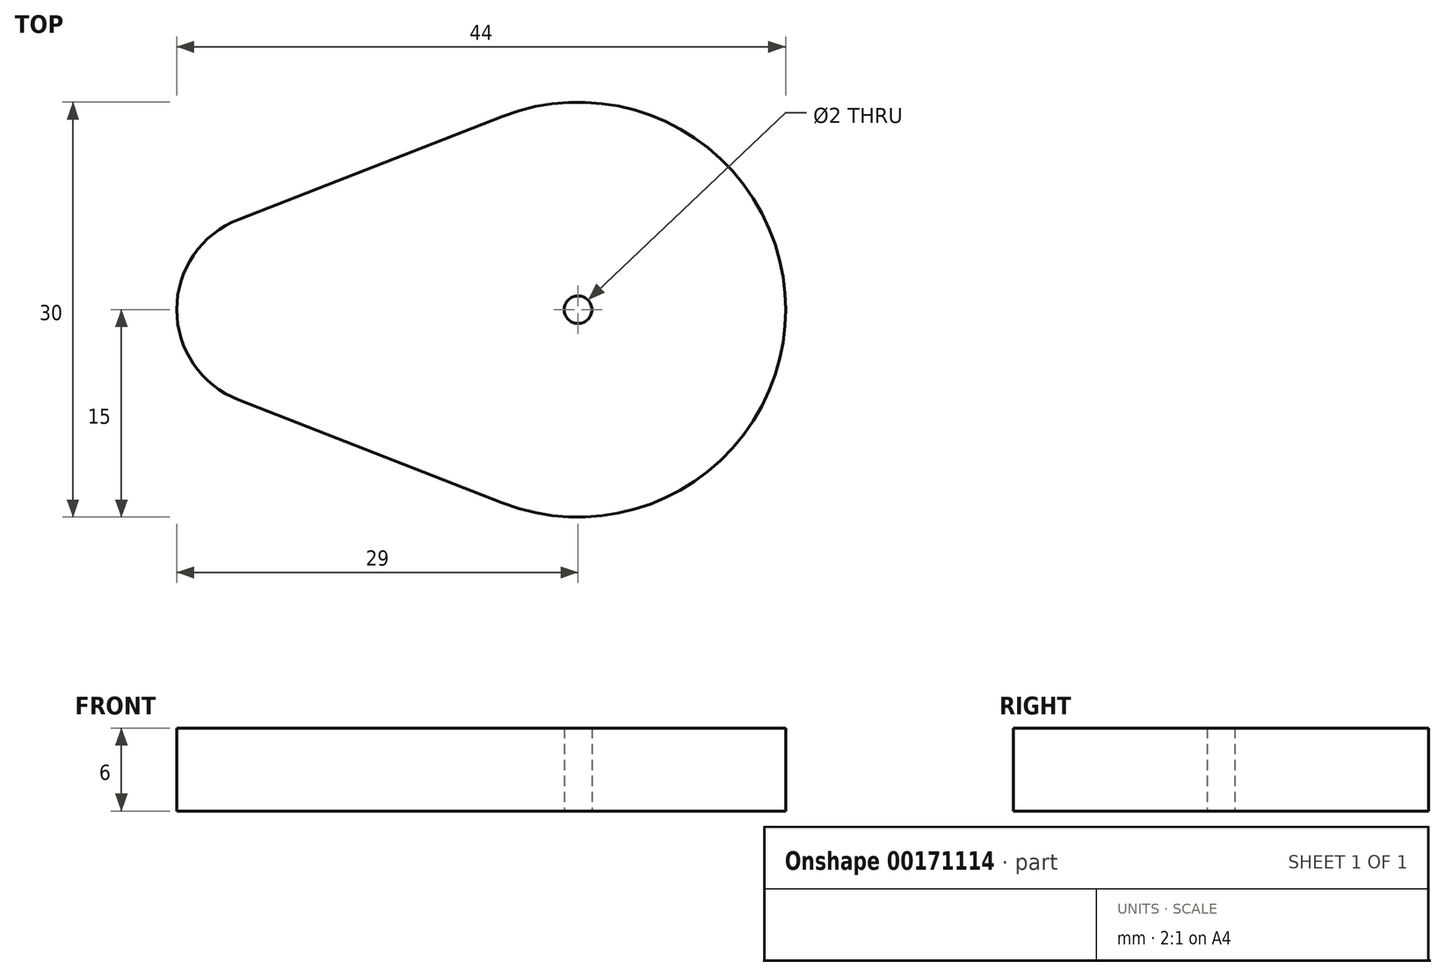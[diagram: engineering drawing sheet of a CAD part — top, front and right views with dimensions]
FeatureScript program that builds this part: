
annotation { "Feature Type Name" : "Feature", "Feature Type Description" : "" }
export const myFeature = defineFeature(function(context is Context, id is Id, definition is map)
    precondition{}
    {
        {
            var Q0;
            Q0=qCreatedBy(makeId("Top.planeOp"),FACE);
            var sketch = newSketch(context, id + "F0", { "sketchPlane" : qUnion([Q0])});
            skArc(sketch, "E0", {"start": v(3.75, 19.65) * mm, "mid": v(-20, 0) * mm, "end": v(3.75, -19.65) * mm});
            skArc(sketch, "E1", {"start": v(42.34, -12.28) * mm, "mid": v(52.5, 0) * mm, "end": v(42.34, 12.28) * mm});
            skLineSegment(sketch, "E2", {"start": v(3.75, 19.65) * mm, "end": v(42.34, 12.28) * mm});
            skLineSegment(sketch, "E3", {"start": v(3.75, -19.65) * mm, "end": v(42.34, -12.28) * mm});
            skCircle(sketch, "E4", {"center": v(0, 0) * mm, "radius": 2 * mm});
            skSolve(sketch);
        }
        {
            var Q0;
            Q0=qCreatedBy(makeId("Top.planeOp"),FACE);
            var sketch = newSketch(context, id + "F1", { "sketchPlane" : qUnion([Q0])});
            skArc(sketch, "E5", {"start": v(-24.55, 6.52) * mm, "mid": v(-29, 0) * mm, "end": v(-24.55, -6.52) * mm});
            skArc(sketch, "E6", {"start": v(-5.45, -13.97) * mm, "mid": v(15, 0) * mm, "end": v(-5.45, 13.97) * mm});
            skLineSegment(sketch, "E7", {"start": v(-24.55, 6.52) * mm, "end": v(-5.45, 13.97) * mm});
            skLineSegment(sketch, "E8", {"start": v(-24.55, -6.52) * mm, "end": v(-5.45, -13.97) * mm});
            skCircle(sketch, "E9", {"center": v(0, 0) * mm, "radius": 1 * mm});
            skSolve(sketch);
        }
        {
            var Q0;
            Q0=makeQuery(id+"F1.imprint","IMPRINT",FACE,{"disambiguationData":[TD([[makeQuery(id+"F1.imprint","IMPRINT",EDGE,{"derivedFrom":sQuery(id+"F1.wireOp",EDGE,"E5")}),1.0]])]});
            extrude(context, id + "F2", {"entities" : qUnion([Q0]), "depth" : 6 * mm});
        }
    });
